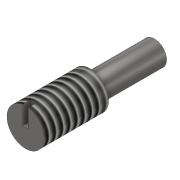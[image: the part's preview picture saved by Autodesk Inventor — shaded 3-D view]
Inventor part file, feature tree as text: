
AUTODESK INVENTOR PART (.ipt)
format: ipt  version: 2017 (Build 210142000, 142)  size: 123,904 bytes
history: native  units: in
note: dims shown in document units (in); Inventor stores cm internally (conversion verified against a paired STEP export)
features: extrude x3, sketch x3, thread x2
ambient origin geometry x8: Origin, YZ Plane, XZ Plane, XY Plane, X Axis, Y Axis, Z Axis, Center Point
bodies: Solid1 (feature_tree)
feature tree (8):
  extrude  "Extrusion1"  Depth=0.375in TaperAngle=0.0deg
  extrude  "Extrusion2"  Depth=0.375in TaperAngle=0.0deg
  thread  "Thread1"  [1 undecoded]
  thread  "Thread2"  [1 undecoded]
  extrude  "Extrusion3"  Depth=0.0312in
  sketch  "Sketch1"  dims[d0=0.216in d1=0.375in d2=0.0in]
  sketch  "Sketch2"  dims[d3=0.141in d4=0.375in d5=0.0in d6=0.375in d7=0.0469in d8=0.375in d9=0.0in]
  sketch  "Sketch3"  dims[d10=0.0156in d11=0.0312in d13=0.0469in d14=0.0in]
note: 2 required parameter values undecoded (feature->parameter linkage not recoverable at this tier; creation-order binding heuristic only, values carry confidence <= 0.55)
